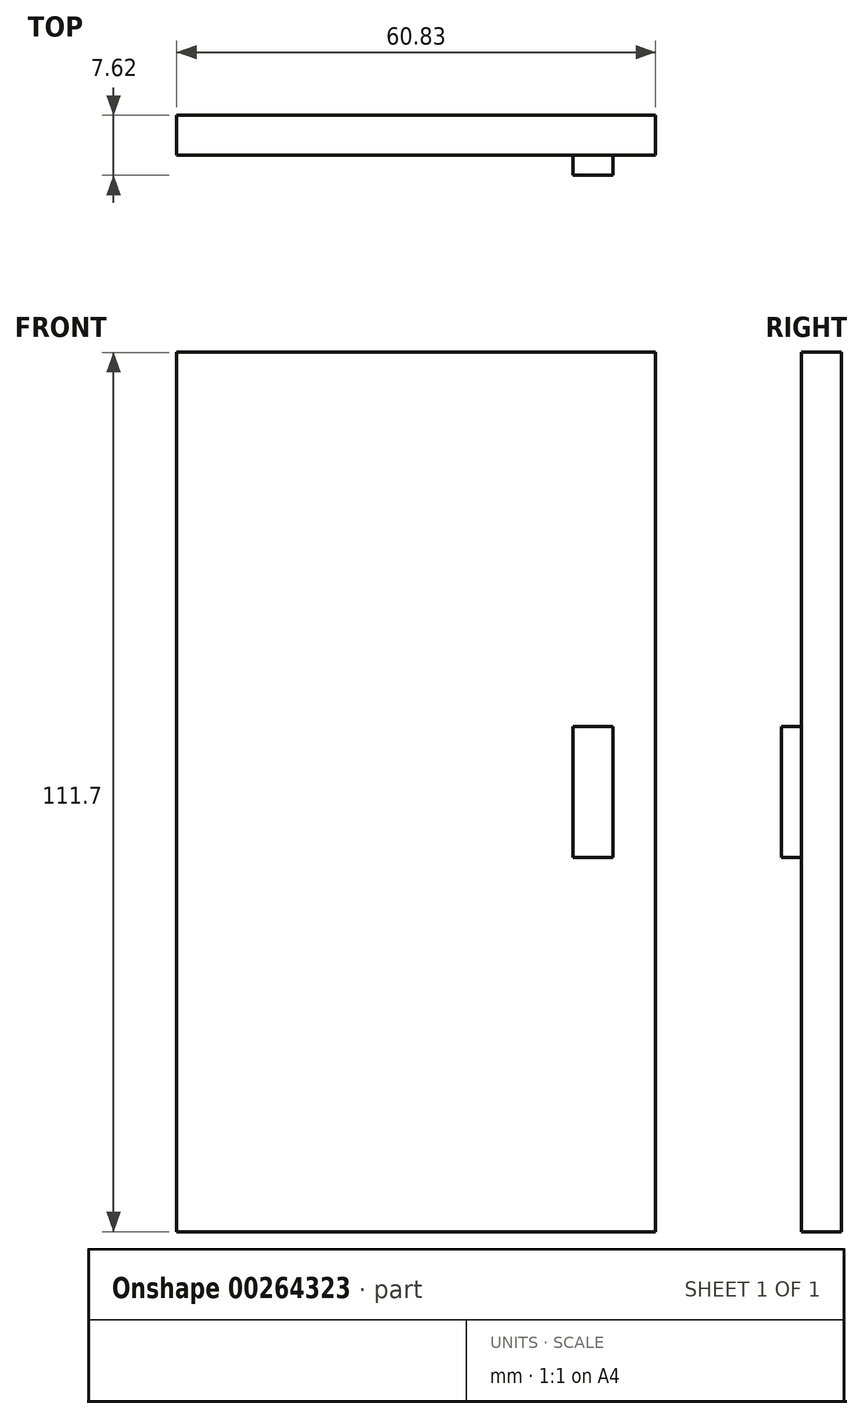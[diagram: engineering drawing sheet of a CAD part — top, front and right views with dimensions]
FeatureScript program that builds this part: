
annotation { "Feature Type Name" : "Feature", "Feature Type Description" : "" }
export const myFeature = defineFeature(function(context is Context, id is Id, definition is map)
    precondition{}
    {
        {
            var Q0;
            Q0=qCreatedBy(makeId("Front.planeOp"),FACE);
            var sketch = newSketch(context, id + "F0", { "sketchPlane" : qUnion([Q0])});
            skLineSegment(sketch, "E0.bottom", {"start": v(32.67, 55.85) * mm, "end": v(-28.16, 55.85) * mm});
            skLineSegment(sketch, "E0.top", {"start": v(32.67, -55.85) * mm, "end": v(-28.16, -55.85) * mm});
            skLineSegment(sketch, "E0.left", {"start": v(32.67, 55.85) * mm, "end": v(32.67, -55.85) * mm});
            skLineSegment(sketch, "E0.right", {"start": v(-28.16, 55.85) * mm, "end": v(-28.16, -55.85) * mm});
            skPoint(sketch, "E0.middle", {"position": v(2.25, 0) * mm});
            skSolve(sketch);
        }
        {
            var Q0;
            Q0=makeQuery(id+"F0.imprint","IMPRINT",FACE,{"disambiguationData":[TD([[makeQuery(id+"F0.imprint","IMPRINT",EDGE,{"derivedFrom":sQuery(id+"F0.wireOp",EDGE,"E0.bottom")}),1.0]])]});
            extrude(context, id + "F1", {"entities" : qUnion([Q0]), "oppositeDirection" : true, "depth" : 5.08 * mm});
        }
        {
            var Q0;
            Q0=makeQuery(id+"F1.opExtrude","CAP_FACE",FACE,{"disambiguationData":[OSD([sQuery(id+"F0.wireOp",EDGE,"E0.bottom"),sQuery(id+"F0.wireOp",EDGE,"E0.top"),sQuery(id+"F0.wireOp",EDGE,"E0.left"),sQuery(id+"F0.wireOp",EDGE,"E0.right")])],"isStart":false});
            var sketch = newSketch(context, id + "F2", { "sketchPlane" : qUnion([Q0])});
            skLineSegment(sketch, "E1.bottom", {"start": v(-22.18, 8.32) * mm, "end": v(-27.28, 8.32) * mm});
            skLineSegment(sketch, "E1.top", {"start": v(-22.18, -8.32) * mm, "end": v(-27.28, -8.32) * mm});
            skLineSegment(sketch, "E1.left", {"start": v(-22.18, 8.32) * mm, "end": v(-22.18, -8.32) * mm});
            skLineSegment(sketch, "E1.right", {"start": v(-27.28, 8.32) * mm, "end": v(-27.28, -8.32) * mm});
            skPoint(sketch, "E1.middle", {"position": v(-24.73, 0) * mm});
            skSolve(sketch);
        }
        {
            var Q0;
            Q0 = qSketchRegion(id + "F2", true);
            extrude(context, id + "F3", {"entities" : qUnion([Q0]), "operationType" : NewBodyOperationType.ADD, "oppositeDirection" : true, "depth" : 7.62 * mm});
        }
    });
